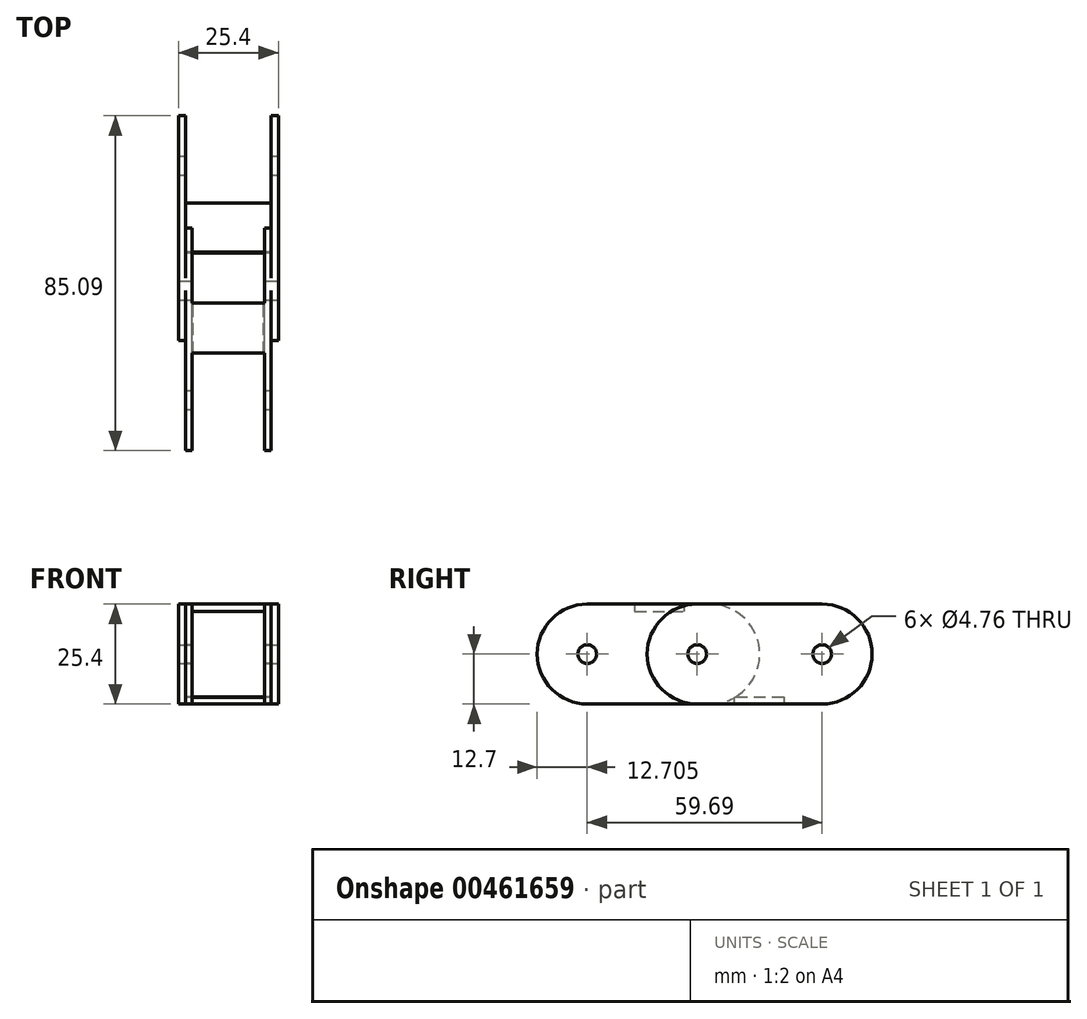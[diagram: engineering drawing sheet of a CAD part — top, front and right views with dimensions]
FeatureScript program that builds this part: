
annotation { "Feature Type Name" : "Feature", "Feature Type Description" : "" }
export const myFeature = defineFeature(function(context is Context, id is Id, definition is map)
    precondition{}
    {
        {
            var Q0;
            Q0=qCreatedBy(makeId("Front.planeOp"),FACE);
            var sketch = newSketch(context, id + "F0", { "sketchPlane" : qUnion([Q0])});
            skLineSegment(sketch, "E0.top", {"start": v(-12.7, 0) * mm, "end": v(12.7, 0) * mm});
            skLineSegment(sketch, "E0.left", {"start": v(-12.7, 25.4) * mm, "end": v(-12.7, 0) * mm});
            skLineSegment(sketch, "E0.right", {"start": v(12.7, 25.4) * mm, "end": v(12.7, 0) * mm});
            skLineSegment(sketch, "E1.0", {"start": v(10.85, 25.4) * mm, "end": v(10.85, 1.85) * mm});
            skLineSegment(sketch, "E1.1", {"start": v(-10.85, 1.85) * mm, "end": v(10.85, 1.85) * mm});
            skLineSegment(sketch, "E1.2", {"start": v(-10.85, 25.4) * mm, "end": v(-10.85, 1.85) * mm});
            skLineSegment(sketch, "E2", {"start": v(-12.7, 25.4) * mm, "end": v(-10.85, 25.4) * mm});
            skLineSegment(sketch, "E3", {"start": v(10.85, 25.4) * mm, "end": v(12.7, 25.4) * mm});
            skSolve(sketch);
        }
        {
            var Q0;
            Q0 = qSketchRegion(id + "F0", true);
            extrude(context, id + "F1", {"entities" : qUnion([Q0]), "depth" : 57.15 * mm, "symmetric" : true});
        }
        {
            var Q0;
            Q0=qCreatedBy(makeId("Right.planeOp"),FACE);
            var sketch = newSketch(context, id + "F2", { "sketchPlane" : qUnion([Q0])});
            skArc(sketch, "E4", {"start": v(-15.88, 25.4) * mm, "mid": v(-28.58, 12.7) * mm, "end": v(-15.88, 0) * mm});
            skArc(sketch, "E5", {"start": v(15.88, 0) * mm, "mid": v(28.58, 12.7) * mm, "end": v(15.88, 25.4) * mm});
            skPoint(sketch, "E6.orphan", {"position": v(28.58, 25.4) * mm});
            skPoint(sketch, "E7.orphan", {"position": v(-28.58, 25.4) * mm});
            skLineSegment(sketch, "E8.0", {"start": v(-28.58, 25.4) * mm, "end": v(-15.88, 25.4) * mm});
            skLineSegment(sketch, "E9.0", {"start": v(28.58, 25.4) * mm, "end": v(28.58, 12.7) * mm});
            skLineSegment(sketch, "E10.0", {"start": v(-28.58, 25.4) * mm, "end": v(-28.58, 12.7) * mm});
            skPoint(sketch, "E11.orphan", {"position": v(-28.58, 0) * mm});
            skPoint(sketch, "E12.orphan", {"position": v(28.58, 0) * mm});
            skCircle(sketch, "E13", {"center": v(-15.88, 12.7) * mm, "radius": 2.38 * mm});
            skCircle(sketch, "E14", {"center": v(15.88, 12.7) * mm, "radius": 2.38 * mm});
            skLineSegment(sketch, "E15.0", {"start": v(-28.58, 0) * mm, "end": v(28.57, 0) * mm});
            skLineSegment(sketch, "E16.0.0", {"start": v(28.58, 0) * mm, "end": v(28.58, 25.4) * mm});
            skLineSegment(sketch, "E16.0.1", {"start": v(28.58, 25.4) * mm, "end": v(15.88, 25.4) * mm});
            skLineSegment(sketch, "E16.0.2", {"start": v(-28.58, 25.4) * mm, "end": v(-28.58, 0) * mm});
            skLineSegment(sketch, "E16.0.3", {"start": v(-28.58, 0) * mm, "end": v(-15.88, 0) * mm});
            skLineSegment(sketch, "E17.trimOffspring", {"start": v(15.88, 0) * mm, "end": v(28.57, 0) * mm});
            skLineSegment(sketch, "E18.trimOffspring", {"start": v(15.88, 25.4) * mm, "end": v(28.57, 25.4) * mm});
            skLineSegment(sketch, "E19.trimOffspring", {"start": v(-15.88, 25.4) * mm, "end": v(-28.58, 25.4) * mm});
            skSolve(sketch);
        }
        {
            var Q0;
            Q0 = qSketchRegion(id + "F2", true);
            extrude(context, id + "F3", {"entities" : qUnion([Q0]), "operationType" : NewBodyOperationType.REMOVE, "oppositeDirection" : true, "depth" : 25.4 * mm, "symmetric" : true});
        }
        {
            var Q0;
            Q0=makeQuery(id+"F1.opExtrude","SWEPT_FACE",FACE,{"disambiguationData":[OSD([sQuery(id+"F0.wireOp",EDGE,"E1.1")])]});
            var sketch = newSketch(context, id + "F4", { "sketchPlane" : qUnion([Q0])});
            skLineSegment(sketch, "E20.bottom", {"start": v(-10.85, 28.72) * mm, "end": v(10.85, 28.72) * mm});
            skLineSegment(sketch, "E20.top", {"start": v(-10.85, 6.35) * mm, "end": v(10.85, 6.35) * mm});
            skLineSegment(sketch, "E20.left", {"start": v(-10.85, 28.72) * mm, "end": v(-10.85, 6.35) * mm});
            skLineSegment(sketch, "E20.right", {"start": v(10.85, 28.72) * mm, "end": v(10.85, 6.35) * mm});
            skLineSegment(sketch, "E21.bottom", {"start": v(-10.85, -6.35) * mm, "end": v(10.85, -6.35) * mm});
            skLineSegment(sketch, "E21.top", {"start": v(-10.85, -28.44) * mm, "end": v(10.85, -28.44) * mm});
            skLineSegment(sketch, "E21.left", {"start": v(-10.85, -6.35) * mm, "end": v(-10.85, -28.44) * mm});
            skLineSegment(sketch, "E21.right", {"start": v(10.85, -6.35) * mm, "end": v(10.85, -28.44) * mm});
            skSolve(sketch);
        }
        {
            var Q0;
            Q0 = qSketchRegion(id + "F4", true);
            extrude(context, id + "F5", {"entities" : qUnion([Q0]), "operationType" : NewBodyOperationType.REMOVE, "oppositeDirection" : true, "depth" : 11.18 * mm});
        }
        {
            var Q0;
            Q0=makeQuery(id+"F5.boolean.opBoolean","MERGE",FACE,{"derivedFrom":[makeQuery(id+"F1.opExtrude","SWEPT_FACE",FACE,{"disambiguationData":[OSD([sQuery(id+"F0.wireOp",EDGE,"E1.2")])]}),makeQuery(id+"F5.opExtrude","SWEPT_FACE",FACE,{"disambiguationData":[OSD([sQuery(id+"F4.wireOp",EDGE,"E21.left")])]})]});
            var sketch = newSketch(context, id + "F6", { "sketchPlane" : qUnion([Q0])});
            skLineSegment(sketch, "E22.bottom", {"start": v(-43.82, 25.4) * mm, "end": v(-12.7, 25.4) * mm});
            skLineSegment(sketch, "E22.top", {"start": v(-43.82, 0) * mm, "end": v(-12.7, 0) * mm});
            skLineSegment(sketch, "E22.left", {"start": v(-56.52, 12.7) * mm, "end": v(-56.52, 12.7) * mm});
            skLineSegment(sketch, "E22.right", {"start": v(0, 12.7) * mm, "end": v(0, 12.7) * mm});
            skPoint(sketch, "E23.visualSharp", {"position": v(0, 25.4) * mm});
            skArc(sketch, "E23.filletArc", {"start": v(0, 12.7) * mm, "mid": v(-3.72, 21.68) * mm, "end": v(-12.7, 25.4) * mm});
            skPoint(sketch, "E24.visualSharp", {"position": v(0, 0) * mm});
            skArc(sketch, "E24.filletArc", {"start": v(-12.7, 0) * mm, "mid": v(-3.72, 3.72) * mm, "end": v(0, 12.7) * mm});
            skPoint(sketch, "E25.visualSharp", {"position": v(-56.52, 0) * mm});
            skArc(sketch, "E25.filletArc", {"start": v(-56.52, 12.7) * mm, "mid": v(-52.8, 3.72) * mm, "end": v(-43.82, 0) * mm});
            skPoint(sketch, "E26.visualSharp", {"position": v(-56.52, 25.4) * mm});
            skArc(sketch, "E26.filletArc", {"start": v(-43.82, 25.4) * mm, "mid": v(-52.8, 21.68) * mm, "end": v(-56.52, 12.7) * mm});
            skCircle(sketch, "E27.0", {"center": v(-15.88, 12.7) * mm, "radius": 2.38 * mm});
            skCircle(sketch, "E28", {"center": v(-43.82, 12.7) * mm, "radius": 2.38 * mm});
            skSolve(sketch);
        }
        {
            var Q0;
            Q0 = qSketchRegion(id + "F6", true);
            var Q1;
            Q1=makeQuery(id+"F5.boolean.opBoolean","MERGE",FACE,{"derivedFrom":[makeQuery(id+"F1.opExtrude","SWEPT_FACE",FACE,{"disambiguationData":[OSD([sQuery(id+"F0.wireOp",EDGE,"E1.0")])]}),makeQuery(id+"F5.opExtrude","SWEPT_FACE",FACE,{"disambiguationData":[OSD([sQuery(id+"F4.wireOp",EDGE,"E20.right")])]}),makeQuery(id+"F5.opExtrude","SWEPT_FACE",FACE,{"disambiguationData":[OSD([sQuery(id+"F4.wireOp",EDGE,"E21.right")])]})]});
            extrude(context, id + "F7", {"entities" : qUnion([Q0]), "operationType" : NewBodyOperationType.ADD, "endBound" : BoundingType.UP_TO_SURFACE, "endBoundEntityFace" : qUnion([Q1]), "depth" : 25.4 * mm});
        }
        {
            var Q0;
            Q0=makeQuery(id+"F7.boolean.opBoolean","MERGE",FACE,{"derivedFrom":[makeQuery(id+"F1.opExtrude","SWEPT_FACE",FACE,{"disambiguationData":[OSD([sQuery(id+"F0.wireOp",EDGE,"E0.top")])]}),makeQuery(id+"F7.opExtrude","SWEPT_FACE",FACE,{"disambiguationData":[OSD([sQuery(id+"F6.wireOp",EDGE,"E22.top")])]})]});
            var sketch = newSketch(context, id + "F8", { "sketchPlane" : qUnion([Q0])});
            skLineSegment(sketch, "E29.bottom", {"start": v(9, 56.46) * mm, "end": v(-9, 56.46) * mm});
            skLineSegment(sketch, "E29.left", {"start": v(9, 56.46) * mm, "end": v(9, 6.5) * mm});
            skLineSegment(sketch, "E29.right", {"start": v(-9, 56.46) * mm, "end": v(-9, 6.5) * mm});
            skPoint(sketch, "E30.orphan", {"position": v(-9, 0) * mm});
            skPoint(sketch, "E31.orphan", {"position": v(9, 0) * mm});
            skLineSegment(sketch, "E32", {"start": v(-9, 6.5) * mm, "end": v(9, 6.5) * mm});
            skSolve(sketch);
        }
        {
            var Q0;
            Q0 = qSketchRegion(id + "F8", true);
            extrude(context, id + "F9", {"entities" : qUnion([Q0]), "operationType" : NewBodyOperationType.REMOVE, "oppositeDirection" : true, "depth" : 23.55 * mm});
        }
        {
            var Q0;
            Q0=qCreatedBy(makeId("Right.planeOp"),FACE);
            var sketch = newSketch(context, id + "F10", { "sketchPlane" : qUnion([Q0])});
            skArc(sketch, "E33.0", {"start": v(-43.82, 25.4) * mm, "mid": v(-56.52, 12.7) * mm, "end": v(-43.82, 0) * mm});
            skLineSegment(sketch, "E34.0", {"start": v(-43.82, 25.4) * mm, "end": v(-31.75, 25.4) * mm});
            skArc(sketch, "E35.0", {"start": v(-12.7, 0) * mm, "mid": v(0, 12.7) * mm, "end": v(-12.7, 25.4) * mm});
            skLineSegment(sketch, "E36.0", {"start": v(-43.82, 0) * mm, "end": v(-12.7, 0) * mm});
            skPoint(sketch, "E37.orphan", {"position": v(-6.1, 1.85) * mm});
            skPoint(sketch, "E38.orphan", {"position": v(-15.88, 0) * mm});
            skPoint(sketch, "E39.orphan", {"position": v(-15.88, 25.4) * mm});
            skLineSegment(sketch, "E40", {"start": v(-19.05, 23.52) * mm, "end": v(-19.05, 25.4) * mm});
            skLineSegment(sketch, "E41", {"start": v(-31.75, 25.4) * mm, "end": v(-31.75, 23.52) * mm});
            skPoint(sketch, "E42.orphan", {"position": v(-19.05, 17.84) * mm});
            skPoint(sketch, "E43.orphan", {"position": v(-12.7, 17.86) * mm});
            skLineSegment(sketch, "E44.0", {"start": v(-31.75, 23.52) * mm, "end": v(-19.05, 23.52) * mm});
            skLineSegment(sketch, "E45.trimOffspring", {"start": v(-19.05, 25.4) * mm, "end": v(-12.7, 25.4) * mm});
            skSolve(sketch);
        }
        {
            var Q0;
            Q0 = qSketchRegion(id + "F10", true);
            extrude(context, id + "F11", {"entities" : qUnion([Q0]), "operationType" : NewBodyOperationType.REMOVE, "depth" : 18.44 * mm, "symmetric" : true});
        }
    });
